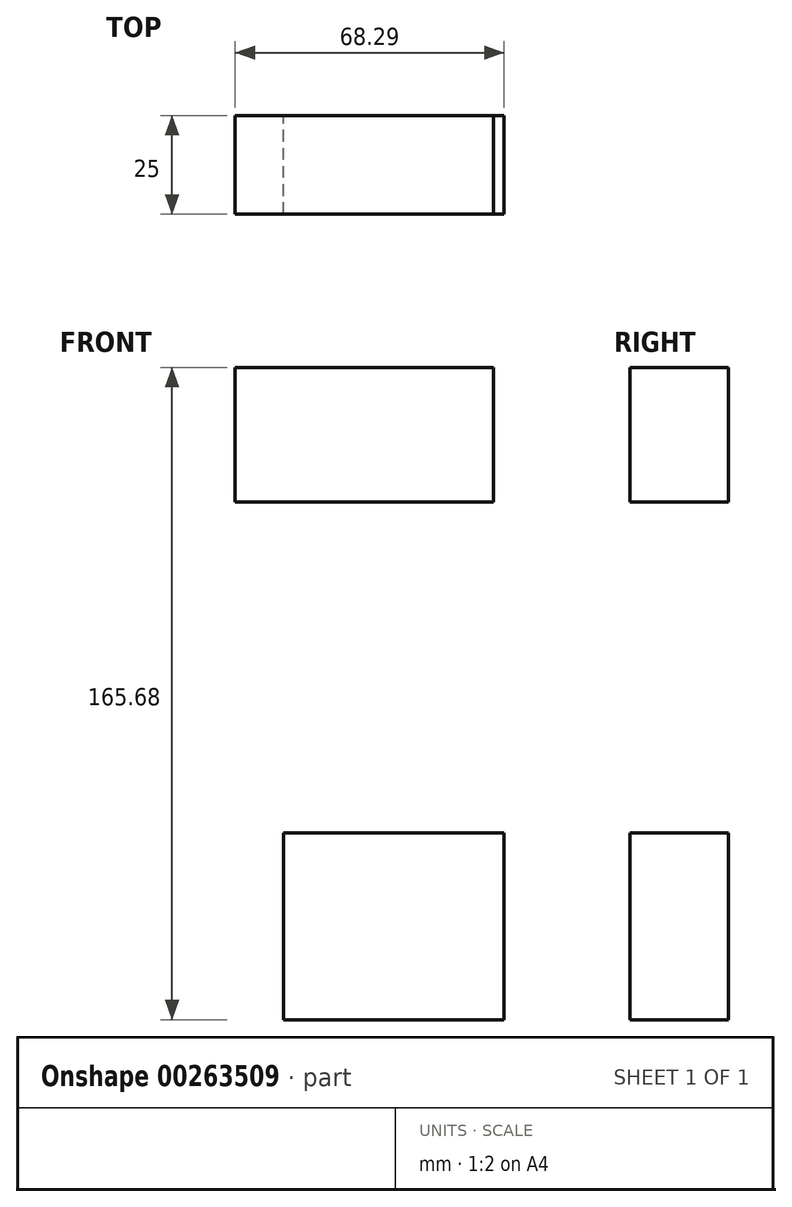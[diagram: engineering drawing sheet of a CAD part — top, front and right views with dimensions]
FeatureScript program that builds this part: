
annotation { "Feature Type Name" : "Feature", "Feature Type Description" : "" }
export const myFeature = defineFeature(function(context is Context, id is Id, definition is map)
    precondition{}
    {
        {
            var Q0;
            Q0=qCreatedBy(makeId("Front.planeOp"),FACE);
            var sketch = newSketch(context, id + "F0", { "sketchPlane" : qUnion([Q0])});
            skLineSegment(sketch, "E0.bottom", {"start": v(30.97, 0) * mm, "end": v(86.95, 0) * mm});
            skLineSegment(sketch, "E0.top", {"start": v(30.97, -47.5) * mm, "end": v(86.95, -47.5) * mm});
            skLineSegment(sketch, "E0.left", {"start": v(30.97, 0) * mm, "end": v(30.97, -47.5) * mm});
            skLineSegment(sketch, "E0.right", {"start": v(86.95, 0) * mm, "end": v(86.95, -47.5) * mm});
            skLineSegment(sketch, "E1.bottom", {"start": v(18.66, 118.18) * mm, "end": v(84.29, 118.18) * mm});
            skLineSegment(sketch, "E1.top", {"start": v(18.66, 84) * mm, "end": v(84.29, 84) * mm});
            skLineSegment(sketch, "E1.left", {"start": v(18.66, 118.18) * mm, "end": v(18.66, 84) * mm});
            skLineSegment(sketch, "E1.right", {"start": v(84.29, 118.18) * mm, "end": v(84.29, 84) * mm});
            skLineSegment(sketch, "E2.bottom", {"start": v(-36.91, 105.21) * mm, "end": v(9.43, 105.21) * mm});
            skLineSegment(sketch, "E2.top", {"start": v(-36.91, 23.64) * mm, "end": v(9.43, 23.64) * mm});
            skLineSegment(sketch, "E2.left", {"start": v(-36.91, 105.21) * mm, "end": v(-36.91, 23.64) * mm});
            skLineSegment(sketch, "E2.right", {"start": v(9.43, 105.21) * mm, "end": v(9.43, 23.64) * mm});
            skSolve(sketch);
        }
        {
            var Q0;
            Q0=makeQuery(id+"F0.imprint","IMPRINT",FACE,{"disambiguationData":[TD([[makeQuery(id+"F0.imprint","IMPRINT",EDGE,{"derivedFrom":sQuery(id+"F0.wireOp",EDGE,"E0.bottom")}),-1.0]])]});
            var Q1;
            Q1=makeQuery(id+"F0.imprint","IMPRINT",FACE,{"disambiguationData":[TD([[makeQuery(id+"F0.imprint","IMPRINT",EDGE,{"derivedFrom":sQuery(id+"F0.wireOp",EDGE,"E1.bottom")}),-1.0]])]});
            extrude(context, id + "F1", {"entities" : qUnion([Q0, Q1]), "depth" : 25 * mm});
        }
    });
